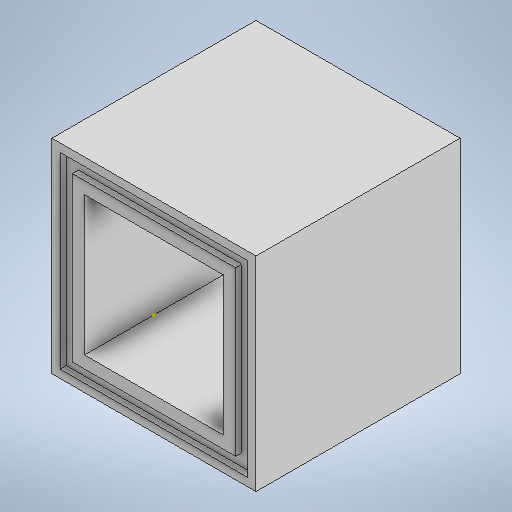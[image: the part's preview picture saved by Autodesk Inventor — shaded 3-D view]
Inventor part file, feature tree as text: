
AUTODESK INVENTOR PART (.ipt)
format: ipt  version: 2025.2 (Build 292293000, 293)  size: 207,872 bytes
history: native  units: mm
features: sketch x5, other x1, extrude x1, sweep x1
ambient origin geometry x8: Origin, YZ Plane, XZ Plane, XY Plane, X Axis, Y Axis, Z Axis, Center Point
bodies: Body1 (feature_tree)
feature tree (8):
  other  "Sólido1"
  extrude  "Extrusão1"  Depth=8.0mm
  sketch  "Esboço2"  dims[d3=50.0mm d4=0.0mm]
  sketch  "Esboço3"  dims[d5=3.5mm]
  sketch  "Esboço8"  dims[d6=3.0mm]
  sweep  "Varredura1"
  sketch  "Esboço1"  dims[d0=50.0mm d2=8.0mm]
  sketch  "Esboço9"  dims[d7=21.5mm d8=0.0mm d9=0.0mm]
